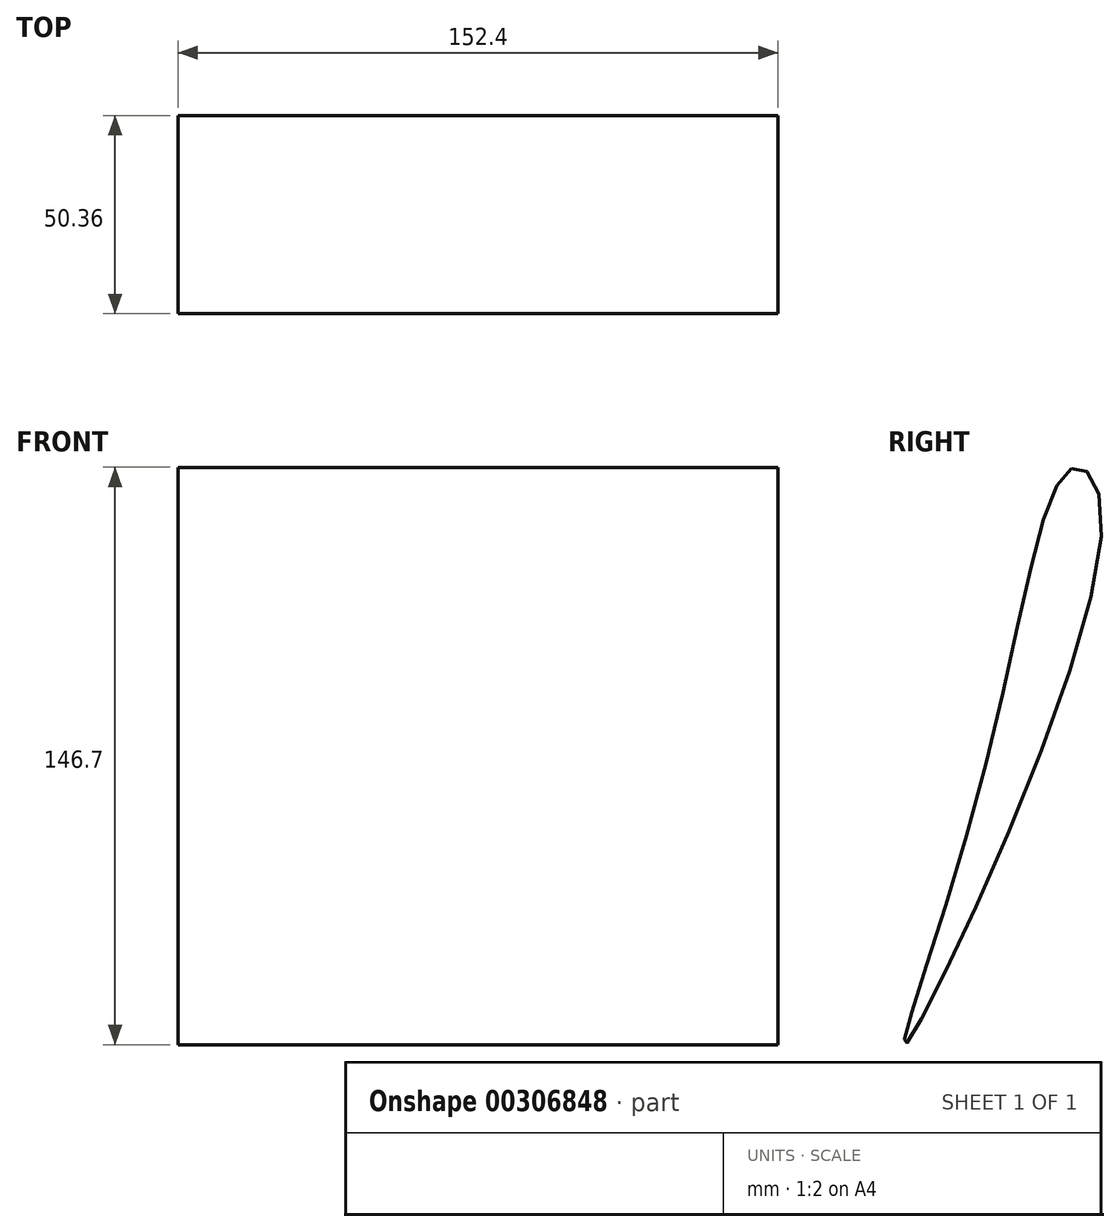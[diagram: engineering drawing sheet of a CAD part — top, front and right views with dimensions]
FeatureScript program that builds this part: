
annotation { "Feature Type Name" : "Feature", "Feature Type Description" : "" }
export const myFeature = defineFeature(function(context is Context, id is Id, definition is map)
    precondition{}
    {
        {
            var Q0;
            Q0=qCreatedBy(makeId("Right.planeOp"),FACE);
            var sketch = newSketch(context, id + "F0", { "sketchPlane" : qUnion([Q0])});
            skFitSpline(sketch, "E0", {"points": [v(39.8, 69.46) * mm, v(47.54, 53.67) * mm, v(-2.03, -76.46) * mm, v(16.63, -11.39) * mm, v(39.8, 69.46) * mm]});
            skSolve(sketch);
        }
        {
            var Q0;
            Q0=makeQuery(id+"F0.imprint","IMPRINT",FACE,{"disambiguationData":[TD([[makeQuery(id+"F0.imprint","IMPRINT",EDGE,{"derivedFrom":sQuery(id+"F0.wireOp",EDGE,"E0")}),-1.0]])]});
            extrude(context, id + "F1", {"entities" : qUnion([Q0]), "depth" : 76.2 * mm, "hasSecondDirection" : true, "secondDirectionOppositeDirection" : true, "secondDirectionDepth" : 76.2 * mm});
        }
    });
